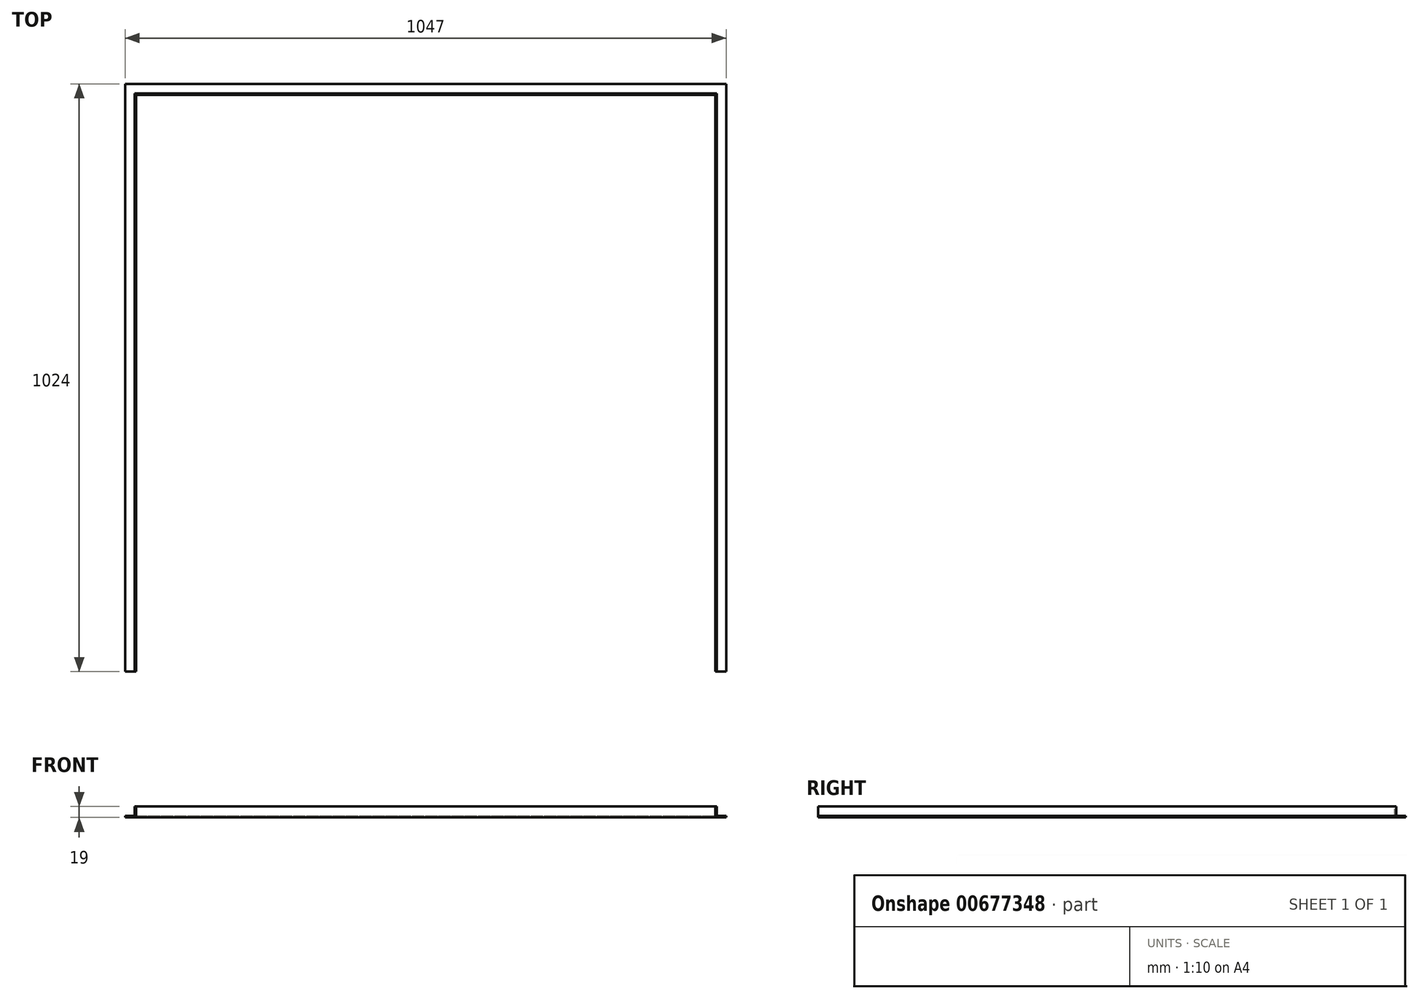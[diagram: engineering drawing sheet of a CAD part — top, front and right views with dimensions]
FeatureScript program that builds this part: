
annotation { "Feature Type Name" : "Feature", "Feature Type Description" : "" }
export const myFeature = defineFeature(function(context is Context, id is Id, definition is map)
    precondition{}
    {
        {
            var Q0;
            Q0=qCreatedBy(makeId("Top.planeOp"),FACE);
            var sketch = newSketch(context, id + "F0", { "sketchPlane" : qUnion([Q0])});
            skLineSegment(sketch, "E0.top", {"start": v(-504.5, 502.5) * mm, "end": v(504.5, 502.5) * mm});
            skLineSegment(sketch, "E0.left", {"start": v(-504.5, -502.5) * mm, "end": v(-504.5, 502.5) * mm});
            skLineSegment(sketch, "E0.right", {"start": v(504.5, -502.5) * mm, "end": v(504.5, 502.5) * mm});
            skPoint(sketch, "E0.middle", {"position": v(0, 0) * mm});
            skSolve(sketch);
        }
        {
            var Q0;
            Q0=qCreatedBy(makeId("Right.planeOp"),FACE);
            var sketch = newSketch(context, id + "F1", { "sketchPlane" : qUnion([Q0])});
            skLineSegment(sketch, "E1", {"start": v(502.5, 0) * mm, "end": v(502.5, 19) * mm});
            skLineSegment(sketch, "E2", {"start": v(502.5, 19) * mm, "end": v(505, 19) * mm});
            skLineSegment(sketch, "E3", {"start": v(505, 19) * mm, "end": v(505, 2.5) * mm});
            skLineSegment(sketch, "E4", {"start": v(505, 2.5) * mm, "end": v(521.5, 2.5) * mm});
            skLineSegment(sketch, "E5", {"start": v(521.5, 2.5) * mm, "end": v(521.5, 0) * mm});
            skLineSegment(sketch, "E6", {"start": v(521.5, 0) * mm, "end": v(502.5, 0) * mm});
            skSolve(sketch);
        }
        {
            var Q0;
            Q0=makeQuery(id+"F1.imprint","IMPRINT",FACE,{"disambiguationData":[TD([[makeQuery(id+"F1.imprint","IMPRINT",EDGE,{"derivedFrom":sQuery(id+"F1.wireOp",EDGE,"E1")}),-1.0]])]});
            var Q1;
            Q1=sQuery(id+"F0.wireOp",EDGE,"E0.top");
            var Q2;
            Q2=sQuery(id+"F0.wireOp",EDGE,"E0.left");
            var Q3;
            Q3=sQuery(id+"F0.wireOp",EDGE,"E0.right");
            sweep(context, id + "F2", {"profiles" : qUnion([Q0]), "path" : qUnion([Q1, Q2, Q3])});
        }
    });
